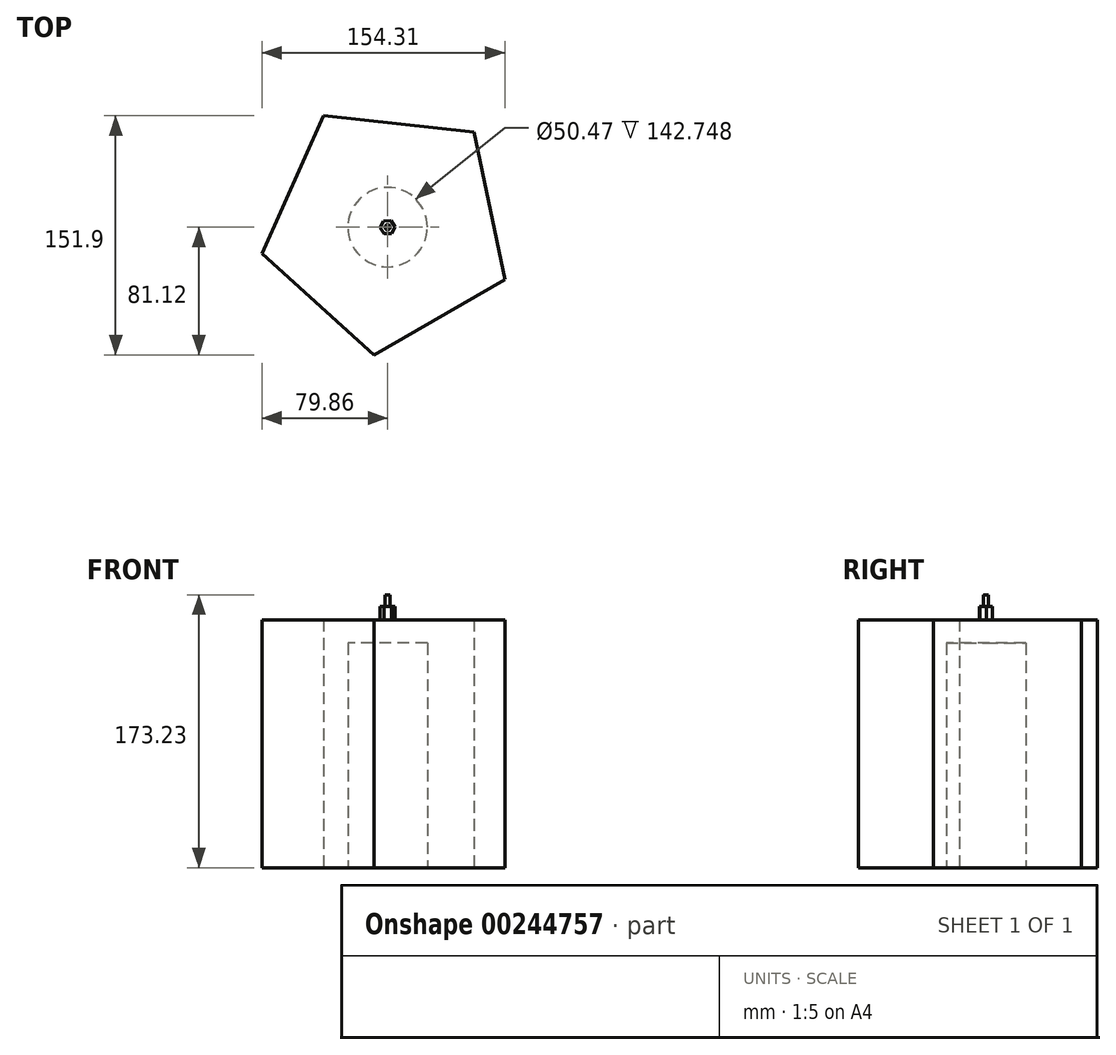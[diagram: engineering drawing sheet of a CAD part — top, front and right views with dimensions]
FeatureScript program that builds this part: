
annotation { "Feature Type Name" : "Feature", "Feature Type Description" : "" }
export const myFeature = defineFeature(function(context is Context, id is Id, definition is map)
    precondition{}
    {
        {
            var Q0;
            Q0=qCreatedBy(makeId("Top.planeOp"),FACE);
            var sketch = newSketch(context, id + "F0", { "sketchPlane" : qUnion([Q0])});
            skCircle(sketch, "E0.cCircle", {"center": v(0, 0) * mm, "radius": 66.01 * mm, "construction": true});
            skLineSegment(sketch, "E0.0", {"start": v(74.45, -33.4) * mm, "end": v(-8.75, -81.12) * mm});
            skLineSegment(sketch, "E0.1", {"start": v(-8.75, -81.12) * mm, "end": v(-79.86, -16.74) * mm});
            skLineSegment(sketch, "E0.2", {"start": v(-79.86, -16.74) * mm, "end": v(-40.6, 70.78) * mm});
            skLineSegment(sketch, "E0.3", {"start": v(-40.6, 70.78) * mm, "end": v(54.77, 60.49) * mm});
            skLineSegment(sketch, "E0.4", {"start": v(54.77, 60.49) * mm, "end": v(74.45, -33.4) * mm});
            skPoint(sketch, "E0.0.midPoint", {"position": v(32.85, -57.26) * mm});
            skSolve(sketch);
        }
        {
            var Q0;
            Q0 = qSketchRegion(id + "F0", true);
            extrude(context, id + "F1", {"entities" : qUnion([Q0]), "depth" : 157.48 * mm});
        }
        {
            var Q0;
            Q0=qCreatedBy(makeId("Top.planeOp"),FACE);
            var sketch = newSketch(context, id + "F2", { "sketchPlane" : qUnion([Q0])});
            skCircle(sketch, "E1", {"center": v(0, 0) * mm, "radius": 25.23 * mm});
            skSolve(sketch);
        }
        {
            var Q0;
            Q0 = qSketchRegion(id + "F2", true);
            extrude(context, id + "F3", {"entities" : qUnion([Q0]), "operationType" : NewBodyOperationType.REMOVE, "depth" : 142.75 * mm});
        }
        {
            var Q0;
            Q0=makeQuery(id+"F1.opExtrude","CAP_FACE",FACE,{"disambiguationData":[OSD([sQuery(id+"F0.wireOp",EDGE,"E0.0"),sQuery(id+"F0.wireOp",EDGE,"E0.1"),sQuery(id+"F0.wireOp",EDGE,"E0.2"),sQuery(id+"F0.wireOp",EDGE,"E0.3"),sQuery(id+"F0.wireOp",EDGE,"E0.4")])],"isStart":false});
            var sketch = newSketch(context, id + "F4", { "sketchPlane" : qUnion([Q0])});
            skCircle(sketch, "E2.cCircle", {"center": v(0, 0) * mm, "radius": 4.07 * mm, "construction": true});
            skLineSegment(sketch, "E2.0", {"start": v(4.7, 0.13) * mm, "end": v(2.46, -4) * mm});
            skLineSegment(sketch, "E2.1", {"start": v(2.46, -4) * mm, "end": v(-2.23, -4.13) * mm});
            skLineSegment(sketch, "E2.2", {"start": v(-2.23, -4.13) * mm, "end": v(-4.7, -0.13) * mm});
            skLineSegment(sketch, "E2.3", {"start": v(-4.7, -0.13) * mm, "end": v(-2.46, 4) * mm});
            skLineSegment(sketch, "E2.4", {"start": v(-2.46, 4) * mm, "end": v(2.23, 4.13) * mm});
            skLineSegment(sketch, "E2.5", {"start": v(2.23, 4.13) * mm, "end": v(4.7, 0.13) * mm});
            skPoint(sketch, "E2.0.midPoint", {"position": v(3.58, -1.93) * mm});
            skSolve(sketch);
        }
        {
            var Q0;
            Q0 = qSketchRegion(id + "F4", true);
            extrude(context, id + "F5", {"entities" : qUnion([Q0]), "operationType" : NewBodyOperationType.ADD, "depth" : 8.64 * mm});
        }
        {
            var Q0;
            Q0=makeQuery(id+"F5.opExtrude","CAP_FACE",FACE,{"disambiguationData":[OSD([sQuery(id+"F4.wireOp",EDGE,"E2.0"),sQuery(id+"F4.wireOp",EDGE,"E2.1"),sQuery(id+"F4.wireOp",EDGE,"E2.2"),sQuery(id+"F4.wireOp",EDGE,"E2.3"),sQuery(id+"F4.wireOp",EDGE,"E2.4"),sQuery(id+"F4.wireOp",EDGE,"E2.5")])],"isStart":false});
            var sketch = newSketch(context, id + "F6", { "sketchPlane" : qUnion([Q0])});
            skCircle(sketch, "E3", {"center": v(0, 0) * mm, "radius": 1.66 * mm});
            skSolve(sketch);
        }
        {
            var Q0;
            Q0 = qSketchRegion(id + "F6", true);
            extrude(context, id + "F7", {"entities" : qUnion([Q0]), "operationType" : NewBodyOperationType.ADD, "depth" : 7.11 * mm});
        }
    });
